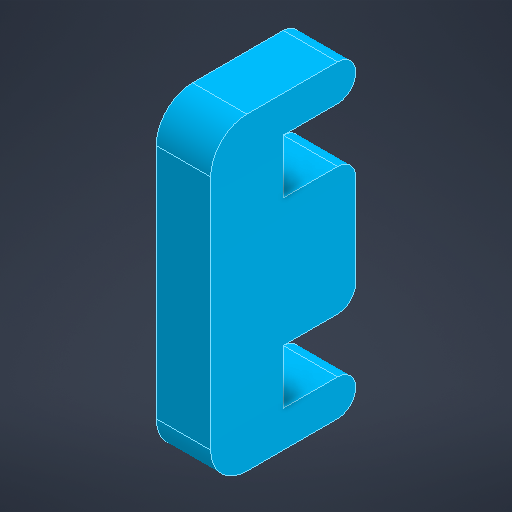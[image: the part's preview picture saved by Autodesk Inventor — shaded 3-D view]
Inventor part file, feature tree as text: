
AUTODESK INVENTOR PART (.ipt)
format: ipt  version: 2025.3 (Build 293356030, 356C)  size: 208,896 bytes
history: native  units: mm
features: fillet x3, other x1, extrude x1, sketch x1
ambient origin geometry x8: Origin, YZ Plane, XZ Plane, XY Plane, X Axis, Y Axis, Z Axis, Center Point
bodies: Body1 (feature_tree)
feature tree (6):
  other  "實體1"
  extrude  "擠出1"  Depth=3.0mm
  fillet  "圓角1"  Radius=7.049mm
  fillet  "圓角2"  Radius=8.0mm
  fillet  "圓角3"  Radius=4.0mm
  sketch  "草圖1"
